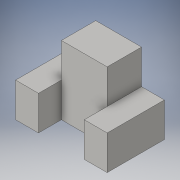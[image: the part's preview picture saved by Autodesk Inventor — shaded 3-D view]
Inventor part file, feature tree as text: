
AUTODESK INVENTOR PART (.ipt)
format: ipt  version: 2016 (Build 200138000, 138)  size: 115,712 bytes
history: native  units: in
note: dims shown in document units (in); Inventor stores cm internally (conversion verified against a paired STEP export)
features: extrude x3, sketch x3
ambient origin geometry x8: Origin, YZ Plane, XZ Plane, XY Plane, X Axis, Y Axis, Z Axis, Center Point
bodies: Solid1 (feature_tree)
feature tree (6):
  extrude  "Extrusion1"  Depth=1.5in
  extrude  "Extrusion2"  Depth=0.5in
  extrude  "Extrusion3"  Depth=0.5in
  sketch  "Sketch1"  dims[d0=2.0in d1=1.5in]
  sketch  "Sketch2"  dims[d2=1.25in d3=0.0in d4=0.5in]
  sketch  "Sketch3"  dims[d5=1.0in d6=0.5in d7=1.5in d8=0.0in d9=0.75in d10=0.75in d11=1.5in d12=0.0in]
